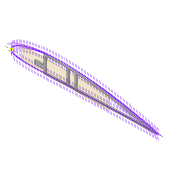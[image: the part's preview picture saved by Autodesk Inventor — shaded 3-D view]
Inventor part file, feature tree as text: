
AUTODESK INVENTOR PART (.ipt)
format: ipt  version: 2022 (Build 260153000, 153)  size: 427,520 bytes
history: native  units: mm
features: extrude x8, sketch x6, projected_geometry x6, fillet x2, shell x1, plane x1
ambient origin geometry x8: Origin, YZ Plane, XZ Plane, XY Plane, X Axis, Y Axis, Z Axis, Center Point
bodies: Solid1 (feature_tree)
feature tree (24):
  extrude  "Extrusion1"  Depth=5.0mm
  shell  "Shell1"  Thickness=2.0mm
  extrude  "Extrusion8"  Depth=5.9mm
  extrude  "Extrusion3"  Depth=10.0mm TaperAngle=0.0deg
  extrude  "Extrusion4"  Depth=2.0mm
  fillet  "Fillet1"  Radius=80.0mm
  extrude  "Extrusion5"  Depth=4.0mm TaperAngle=0.0deg
  plane  "Work Plane2"
  extrude  "Extrusion10"  Depth=0.2mm
  fillet  "Fillet2"  Radius=4.0mm
  extrude  "Extrusion9"  Depth=0.2mm
  extrude  "Extrusion11"  Depth=0.2mm
  sketch  "Sketch3"  dims[d0=4.0mm d1=0.0mm d2=5.0mm d7=2.0mm]
  sketch  "Sketch8"  dims[d8=2.0mm d9=5.9mm]
  sketch  "Sketch9"  dims[d13=10.0mm d14=0.0mm d16=10.0mm d17=0.0mm]
  projected_geometry  "Projected Loop4"
  projected_geometry  "Projected Loop10"
  sketch  "Sketch24"  dims[d22=4.0mm d23=0.0mm d31=2.0mm d62=80.0mm]
  projected_geometry  "Projected Loop11"
  projected_geometry  "Projected Loop12"
  projected_geometry  "Projected Loop13"
  sketch  "Sketch27"  dims[d63=6.0mm d64=4.0mm d65=0.0mm]
  projected_geometry  "Projected Loop14"
  sketch  "Sketch28"  dims[d66=3.0mm d67=12.0mm d72=4.0mm d73=0.0mm d74=12.0mm d75=30.0mm d76=3.05mm d77=5.0mm d78=10.0mm d79=0.0mm d80=2.0mm d84=6.0mm d85=260.0mm d86=6.0mm d87=20.0mm d88=2.1mm d89=2.1mm d90=3.0mm d91=3.0mm d92=0.2mm d93=10.0mm d94=0.0mm]
